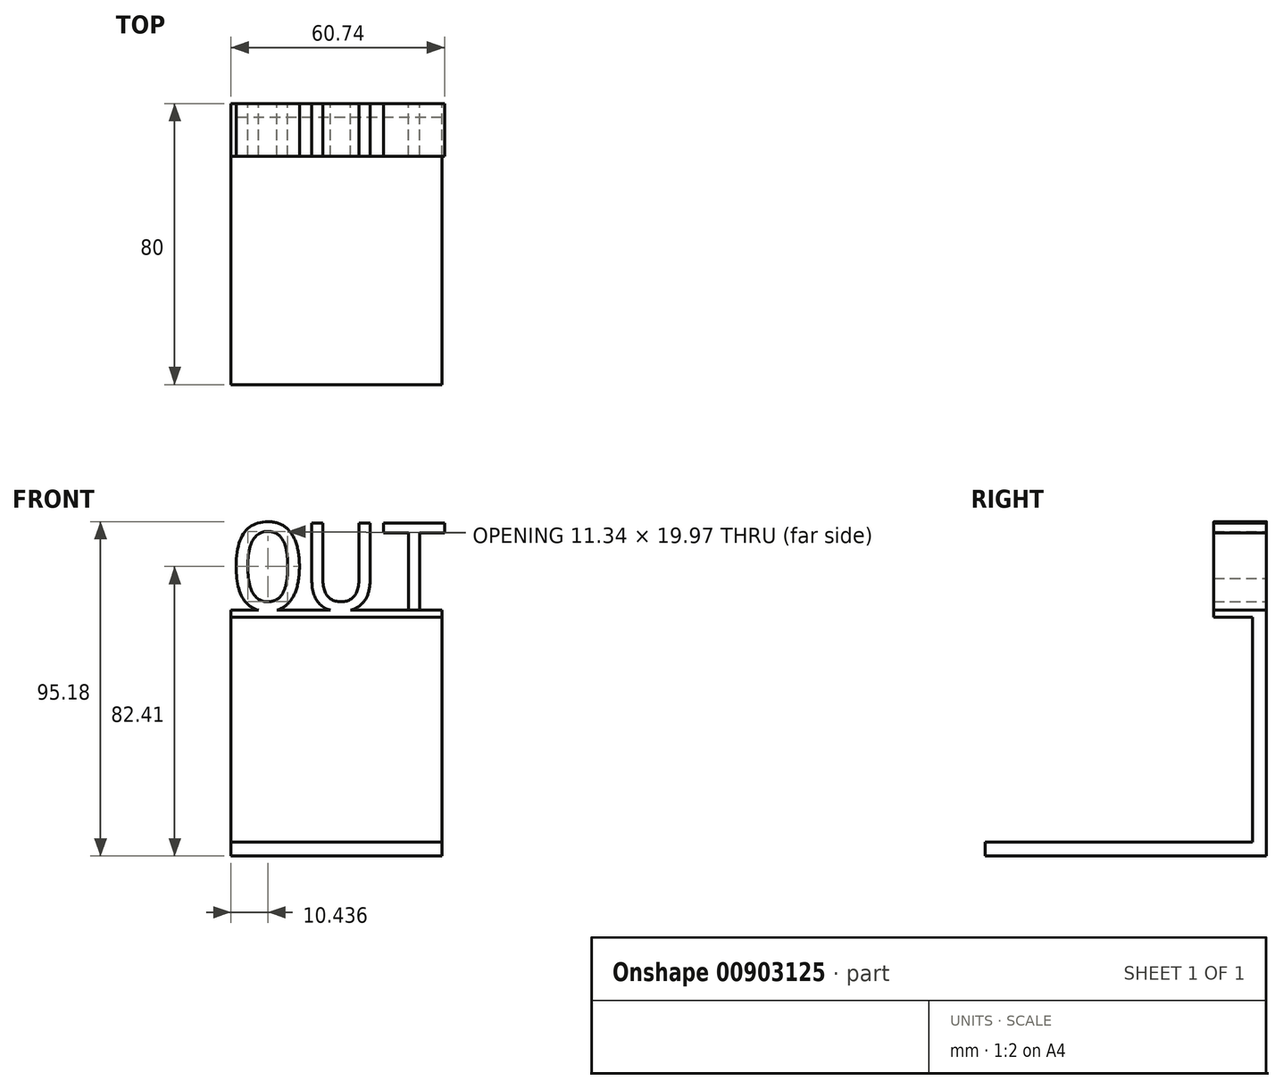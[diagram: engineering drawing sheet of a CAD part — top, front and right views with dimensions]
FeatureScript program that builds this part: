
annotation { "Feature Type Name" : "Feature", "Feature Type Description" : "" }
export const myFeature = defineFeature(function(context is Context, id is Id, definition is map)
    precondition{}
    {
        {
            var Q0;
            Q0=qCreatedBy(makeId("Front.planeOp"),FACE);
            var sketch = newSketch(context, id + "F0", { "sketchPlane" : qUnion([Q0])});
            skLineSegment(sketch, "E0.bottom", {"start": v(-28.33, 24.57) * mm, "end": v(31.67, 24.57) * mm});
            skLineSegment(sketch, "E0.top", {"start": v(-28.33, -45.43) * mm, "end": v(31.67, -45.43) * mm});
            skLineSegment(sketch, "E0.left", {"start": v(-28.33, 24.57) * mm, "end": v(-28.33, -45.43) * mm});
            skLineSegment(sketch, "E0.right", {"start": v(31.67, 24.57) * mm, "end": v(31.67, -45.43) * mm});
            skSolve(sketch);
        }
        {
            var Q0;
            Q0=makeQuery(id+"F0.imprint","IMPRINT",FACE,{"disambiguationData":[TD([[makeQuery(id+"F0.imprint","IMPRINT",EDGE,{"derivedFrom":sQuery(id+"F0.wireOp",EDGE,"E0.bottom")}),-1.0]])]});
            extrude(context, id + "F1", {"entities" : qUnion([Q0]), "depth" : 4 * mm, "offsetDistance" : 25 * mm});
        }
        {
            var Q0;
            Q0=qCreatedBy(makeId("Front.planeOp"),FACE);
            var sketch = newSketch(context, id + "F2", { "sketchPlane" : qUnion([Q0])});
            skLineSegment(sketch, "E1.bottom", {"start": v(-28.33, 24.57) * mm, "end": v(31.67, 24.57) * mm});
            skLineSegment(sketch, "E1.top", {"start": v(-28.33, 22.57) * mm, "end": v(31.67, 22.57) * mm});
            skLineSegment(sketch, "E1.left", {"start": v(-28.33, 24.57) * mm, "end": v(-28.33, 22.57) * mm});
            skLineSegment(sketch, "E1.right", {"start": v(31.67, 24.57) * mm, "end": v(31.67, 22.57) * mm});
            skSolve(sketch);
        }
        {
            var Q0;
            Q0=qSketchRegion(id+"F2",true);
            extrude(context, id + "F3", {"entities" : qUnion([Q0]), "operationType" : NewBodyOperationType.ADD, "depth" : 15 * mm, "offsetDistance" : 25 * mm});
        }
        {
            var Q0;
            Q0=qCreatedBy(makeId("Front.planeOp"),FACE);
            var sketch = newSketch(context, id + "F4", { "sketchPlane" : qUnion([Q0])});
            skLineSegment(sketch, "E2.bottom", {"start": v(-28.33, -41.43) * mm, "end": v(31.67, -41.43) * mm});
            skLineSegment(sketch, "E2.top", {"start": v(-28.33, -45.43) * mm, "end": v(31.67, -45.43) * mm});
            skLineSegment(sketch, "E2.left", {"start": v(-28.33, -41.43) * mm, "end": v(-28.33, -45.43) * mm});
            skLineSegment(sketch, "E2.right", {"start": v(31.67, -41.43) * mm, "end": v(31.67, -45.43) * mm});
            skSolve(sketch);
        }
        {
            var Q0;
            Q0=qSketchRegion(id+"F4",true);
            extrude(context, id + "F5", {"entities" : qUnion([Q0]), "operationType" : NewBodyOperationType.ADD, "depth" : 80 * mm, "offsetDistance" : 25 * mm});
        }
        {
            var Q0;
            Q0=qCreatedBy(makeId("Front.planeOp"),FACE);
            var sketch = newSketch(context, id + "F6", { "sketchPlane" : qUnion([Q0])});
            skText(sketch, "E3", { "text": "OUT", "fontName": "DroidSansMono.ttf"});
            const initialGuessF6  = {"E3": [-0.02833, 0.02457, 1, 0, 0.025]};
            skSetInitialGuess(sketch, initialGuessF6);
            skSolve(sketch);
        }
        {
            var Q0;
            Q0=qSketchRegion(id+"F6",true);
            extrude(context, id + "F7", {"entities" : qUnion([Q0]), "operationType" : NewBodyOperationType.ADD, "depth" : 15 * mm, "offsetDistance" : 25 * mm});
        }
    });
